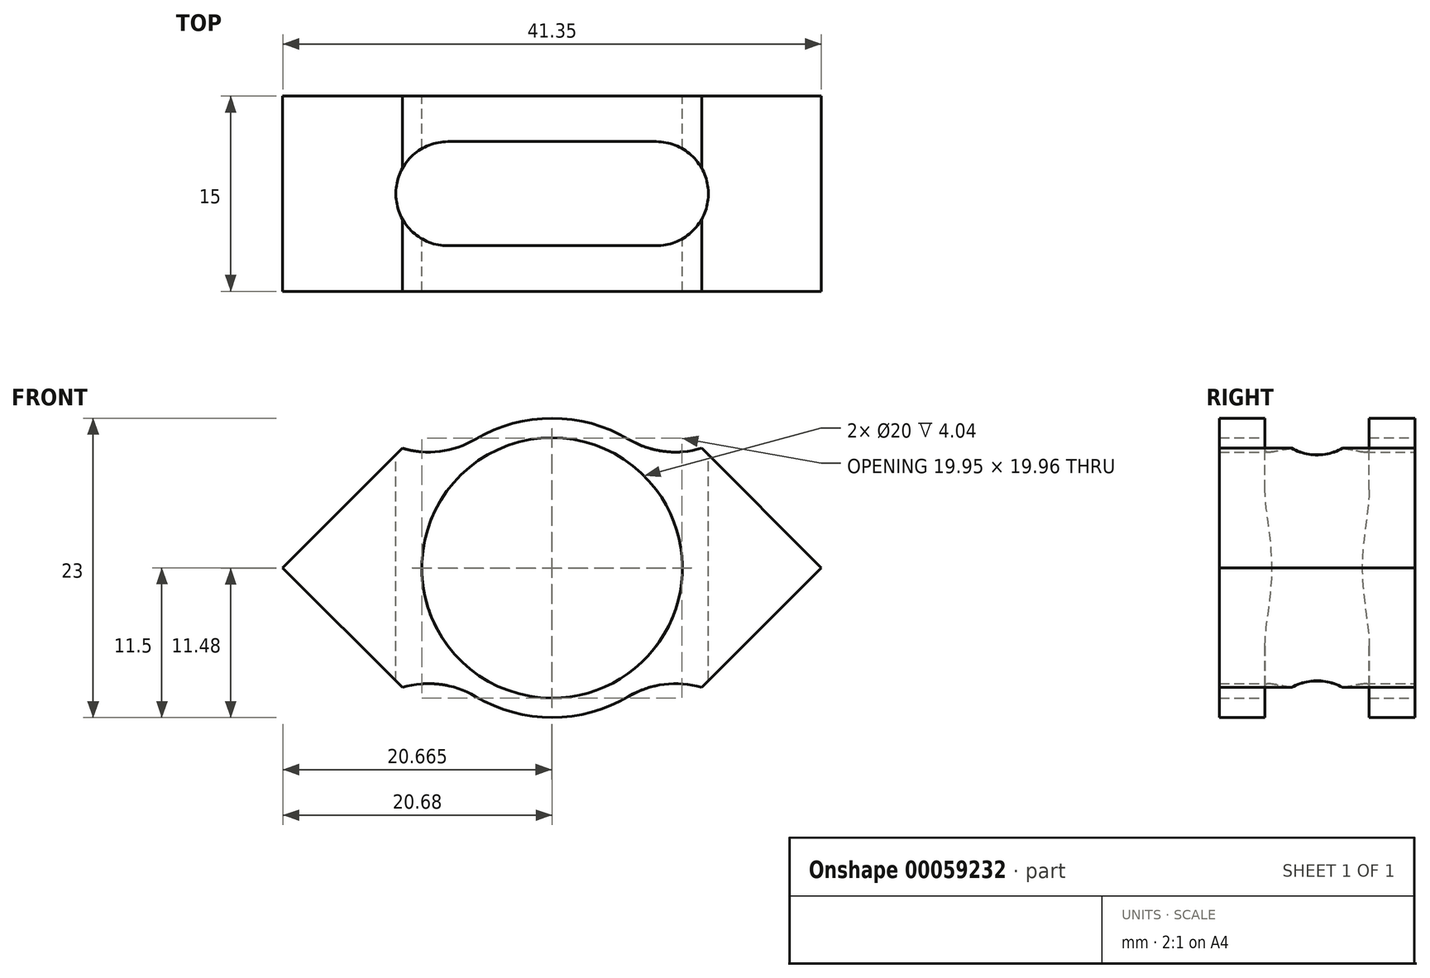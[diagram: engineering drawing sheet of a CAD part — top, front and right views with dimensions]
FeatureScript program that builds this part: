
annotation { "Feature Type Name" : "Feature", "Feature Type Description" : "" }
export const myFeature = defineFeature(function(context is Context, id is Id, definition is map)
    precondition{}
    {
        {
            var Q0;
            Q0=qCreatedBy(makeId("Front.planeOp"),FACE);
            var sketch = newSketch(context, id + "F0", { "sketchPlane" : qUnion([Q0])});
            skCircle(sketch, "E0", {"center": v(0, 0) * mm, "radius": 10 * mm});
            skCircle(sketch, "E1", {"center": v(0, 0) * mm, "radius": 11.5 * mm, "construction": true});
            skLineSegment(sketch, "E2", {"start": v(-11.5, 9.2) * mm, "end": v(-20.68, 0) * mm});
            skLineSegment(sketch, "E3", {"start": v(-20.68, 0) * mm, "end": v(-11.5, -9.2) * mm});
            skLineSegment(sketch, "E4", {"start": v(11.48, 9.2) * mm, "end": v(20.67, 0) * mm});
            skLineSegment(sketch, "E5", {"start": v(20.67, 0) * mm, "end": v(11.48, -9.2) * mm});
            skArc(sketch, "E6", {"start": v(5.88, 9.88) * mm, "mid": v(8.6, 8.95) * mm, "end": v(11.48, 9.2) * mm});
            skArc(sketch, "E7", {"start": v(11.48, -9.2) * mm, "mid": v(8.6, -8.95) * mm, "end": v(5.88, -9.88) * mm});
            skArc(sketch, "E8", {"start": v(-11.5, 9.2) * mm, "mid": v(-8.62, 8.95) * mm, "end": v(-5.89, 9.88) * mm});
            skArc(sketch, "E9", {"start": v(-5.89, -9.88) * mm, "mid": v(-8.62, -8.95) * mm, "end": v(-11.5, -9.2) * mm});
            skArc(sketch, "E10", {"start": v(5.88, 9.88) * mm, "mid": v(0, 11.5) * mm, "end": v(-5.89, 9.88) * mm});
            skArc(sketch, "E11", {"start": v(-5.89, -9.88) * mm, "mid": v(0, -11.5) * mm, "end": v(5.88, -9.88) * mm});
            skSolve(sketch);
        }
        {
            var Q0;
            Q0=makeQuery(id+"F0.imprint","IMPRINT",FACE,{"disambiguationData":[TD([[makeQuery(id+"F0.imprint","IMPRINT",EDGE,{"derivedFrom":sQuery(id+"F0.wireOp",EDGE,"E0")}),-1.0]])]});
            extrude(context, id + "F1", {"entities" : qUnion([Q0]), "endBound" : BoundingType.SYMMETRIC, "depth" : 15 * mm});
        }
        {
            var Q0;
            Q0=qCreatedBy(makeId("Top.planeOp"),FACE);
            var sketch = newSketch(context, id + "F2", { "sketchPlane" : qUnion([Q0])});
            skArc(sketch, "E12", {"start": v(-8, 4) * mm, "mid": v(-12, 0) * mm, "end": v(-8, -4) * mm});
            skLineSegment(sketch, "E13", {"start": v(-8, 4) * mm, "end": v(8, 4) * mm});
            skLineSegment(sketch, "E14", {"start": v(-8, -4) * mm, "end": v(8, -4) * mm});
            skArc(sketch, "E15", {"start": v(8, -4) * mm, "mid": v(12, 0) * mm, "end": v(8, 4) * mm});
            skSolve(sketch);
        }
        {
            var Q0;
            Q0 = qSketchRegion(id + "F2", true);
            extrude(context, id + "F3", {"entities" : qUnion([Q0]), "operationType" : NewBodyOperationType.REMOVE, "endBound" : BoundingType.SYMMETRIC, "oppositeDirection" : true, "depth" : 50 * mm});
        }
    });
